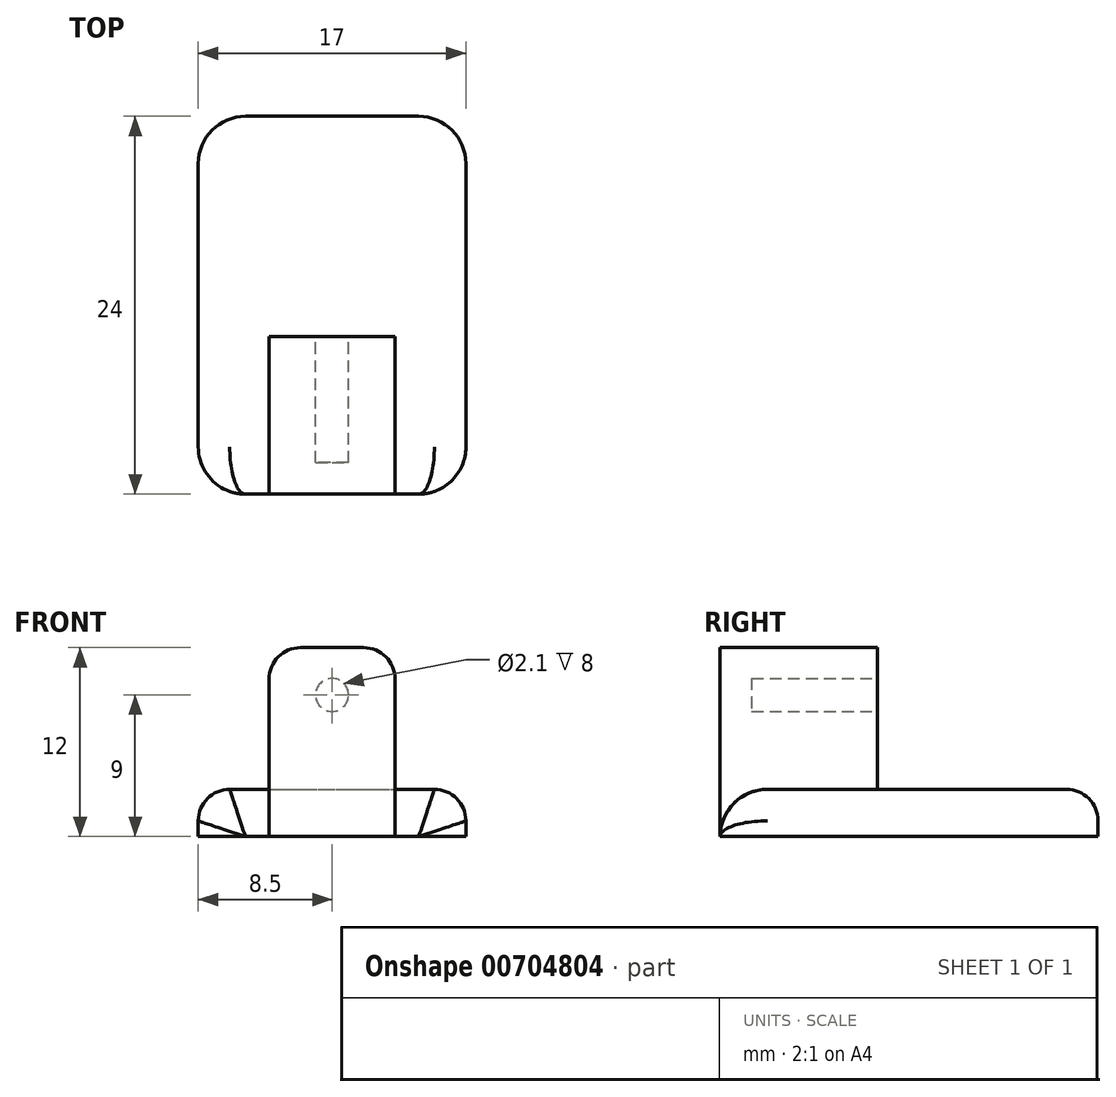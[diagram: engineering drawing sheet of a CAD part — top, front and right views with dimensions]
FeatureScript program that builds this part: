
annotation { "Feature Type Name" : "Feature", "Feature Type Description" : "" }
export const myFeature = defineFeature(function(context is Context, id is Id, definition is map)
    precondition{}
    {
        {
            var Q0;
            Q0=qCreatedBy(makeId("Top.planeOp"),FACE);
            var sketch = newSketch(context, id + "F0", { "sketchPlane" : qUnion([Q0])});
            skLineSegment(sketch, "E0.bottom", {"start": v(-8.5, 12) * mm, "end": v(8.5, 12) * mm});
            skLineSegment(sketch, "E0.top", {"start": v(-8.5, -12) * mm, "end": v(8.5, -12) * mm});
            skLineSegment(sketch, "E0.left", {"start": v(-8.5, 12) * mm, "end": v(-8.5, -12) * mm});
            skLineSegment(sketch, "E0.right", {"start": v(8.5, 12) * mm, "end": v(8.5, -12) * mm});
            skPoint(sketch, "E0.middle", {"position": v(0, 0) * mm});
            skSolve(sketch);
        }
        {
            var Q0;
            Q0=makeQuery(id+"F0.imprint","IMPRINT",FACE,{"disambiguationData":[TD([[makeQuery(id+"F0.imprint","IMPRINT",EDGE,{"derivedFrom":sQuery(id+"F0.wireOp",EDGE,"E0.bottom")}),-1.0]])]});
            extrude(context, id + "F1", {"entities" : qUnion([Q0]), "depth" : 3 * mm, "offsetDistance" : 25 * mm});
        }
        {
            var Q0;
            Q0=makeQuery(id+"F1.opExtrude","CAP_FACE",FACE,{"disambiguationData":[OSD([sQuery(id+"F0.wireOp",EDGE,"E0.bottom"),sQuery(id+"F0.wireOp",EDGE,"E0.top"),sQuery(id+"F0.wireOp",EDGE,"E0.left"),sQuery(id+"F0.wireOp",EDGE,"E0.right")])],"isStart":false});
            var sketch = newSketch(context, id + "F2", { "sketchPlane" : qUnion([Q0])});
            skLineSegment(sketch, "E1.bottom", {"start": v(-4, -12) * mm, "end": v(4, -12) * mm});
            skLineSegment(sketch, "E1.top", {"start": v(-4, -2) * mm, "end": v(4, -2) * mm});
            skLineSegment(sketch, "E1.left", {"start": v(-4, -12) * mm, "end": v(-4, -2) * mm});
            skLineSegment(sketch, "E1.right", {"start": v(4, -12) * mm, "end": v(4, -2) * mm});
            skPoint(sketch, "E1.middle", {"position": v(0, -7) * mm});
            skSolve(sketch);
        }
        {
            var Q0;
            Q0=makeQuery(id+"F2.imprint","IMPRINT",FACE,{"disambiguationData":[TD([[makeQuery(id+"F2.imprint","IMPRINT",EDGE,{"derivedFrom":sQuery(id+"F2.wireOp",EDGE,"E1.bottom")}),1.0]])]});
            extrude(context, id + "F3", {"entities" : qUnion([Q0]), "operationType" : NewBodyOperationType.ADD, "depth" : 9 * mm, "offsetDistance" : 25 * mm});
        }
        {
            var Q0;
            Q0=makeQuery(id+"F3.opExtrude","SWEPT_FACE",FACE,{"disambiguationData":[OSD([sQuery(id+"F2.wireOp",EDGE,"E1.top")])]});
            var sketch = newSketch(context, id + "F4", { "sketchPlane" : qUnion([Q0])});
            skCircle(sketch, "E2", {"center": v(0, 9) * mm, "radius": 1.05 * mm});
            skSolve(sketch);
        }
        {
            var Q0;
            Q0=makeQuery(id+"F4.imprint","IMPRINT",FACE,{"disambiguationData":[TD([[makeQuery(id+"F4.imprint","IMPRINT",EDGE,{"derivedFrom":sQuery(id+"F4.wireOp",EDGE,"E2")}),1.0]])]});
            extrude(context, id + "F5", {"entities" : qUnion([Q0]), "operationType" : NewBodyOperationType.REMOVE, "oppositeDirection" : true, "depth" : 8 * mm, "offsetDistance" : 25 * mm});
        }
        {
            var Q0;
            Q0=makeQuery(id+"F3.opExtrude","CAP_EDGE",EDGE,{"disambiguationData":[OSD([sQuery(id+"F2.wireOp",EDGE,"E1.right")])],"isStart":true});
            var Q1;
            Q1=makeQuery(id+"F3.opExtrude","CAP_EDGE",EDGE,{"disambiguationData":[OSD([sQuery(id+"F2.wireOp",EDGE,"E1.right")])],"isStart":false});
            var Q2;
            Q2=makeQuery(id+"F3.opExtrude","CAP_EDGE",EDGE,{"disambiguationData":[OSD([sQuery(id+"F2.wireOp",EDGE,"E1.left")])],"isStart":false});
            var Q3;
            Q3=makeQuery(id+"F3.opExtrude","CAP_EDGE",EDGE,{"disambiguationData":[OSD([sQuery(id+"F2.wireOp",EDGE,"E1.left")])],"isStart":true});
            var Q4;
            Q4=makeQuery(id+"F1.opExtrude","CAP_EDGE",EDGE,{"disambiguationData":[OSD([sQuery(id+"F0.wireOp",EDGE,"E0.right")])],"isStart":false});
            var Q5;
            Q5=makeQuery(id+"F1.opExtrude","CAP_EDGE",EDGE,{"disambiguationData":[OSD([sQuery(id+"F0.wireOp",EDGE,"E0.left")])],"isStart":false});
            var Q6;
            Q6=makeQuery(id+"F1.opExtrude","CAP_EDGE",EDGE,{"disambiguationData":[OSD([sQuery(id+"F0.wireOp",EDGE,"E0.bottom")])],"isStart":false});
            fillet(context, id + "F6", {"entities" : qUnion([Q0, Q1, Q2, Q3, Q4, Q5, Q6]), "radius" : 2 * mm, "tangentPropagation" : true, "allowEdgeOverflow" : false});
        }
        {
            var Q0;
            Q0=makeQuery(id+"F1.opExtrude","SWEPT_EDGE",EDGE,{"disambiguationData":[OSD([sQuery(id+"F0.wireOp",EDGE,"E0.bottom"),sQuery(id+"F0.wireOp",EDGE,"E0.right")])]});
            var Q1;
            Q1=makeQuery(id+"F1.opExtrude","SWEPT_EDGE",EDGE,{"disambiguationData":[OSD([sQuery(id+"F0.wireOp",EDGE,"E0.bottom"),sQuery(id+"F0.wireOp",EDGE,"E0.left")])]});
            var Q2;
            Q2=makeQuery(id+"F1.opExtrude","SWEPT_EDGE",EDGE,{"disambiguationData":[OSD([sQuery(id+"F0.wireOp",EDGE,"E0.top"),sQuery(id+"F0.wireOp",EDGE,"E0.left")])]});
            var Q3;
            Q3=makeQuery(id+"F6.opFillet","BLEND_EDGE",EDGE,{"blendedFrom":[makeQuery(id+"F1.opExtrude","CAP_EDGE",EDGE,{"disambiguationData":[OSD([sQuery(id+"F0.wireOp",EDGE,"E0.right")])],"isStart":false}),makeQuery(id+"F3.boolean.opBoolean","MERGE",FACE,{"derivedFrom":[makeQuery(id+"F1.opExtrude","SWEPT_FACE",FACE,{"disambiguationData":[OSD([sQuery(id+"F0.wireOp",EDGE,"E0.top")])]}),makeQuery(id+"F3.opExtrude","SWEPT_FACE",FACE,{"disambiguationData":[OSD([sQuery(id+"F2.wireOp",EDGE,"E1.bottom")])]})]})],"blendedInto":[makeQuery(id+"F3.boolean.opBoolean","MERGE",FACE,{"derivedFrom":[makeQuery(id+"F1.opExtrude","SWEPT_FACE",FACE,{"disambiguationData":[OSD([sQuery(id+"F0.wireOp",EDGE,"E0.top")])]}),makeQuery(id+"F3.opExtrude","SWEPT_FACE",FACE,{"disambiguationData":[OSD([sQuery(id+"F2.wireOp",EDGE,"E1.bottom")])]})]})]});
            var Q4;
            Q4=makeQuery(id+"F1.opExtrude","SWEPT_EDGE",EDGE,{"disambiguationData":[OSD([sQuery(id+"F0.wireOp",EDGE,"E0.top"),sQuery(id+"F0.wireOp",EDGE,"E0.right")])]});
            var Q5;
            Q5=makeQuery(id+"F6.opFillet","BLEND_EDGE",EDGE,{"blendedFrom":[makeQuery(id+"F1.opExtrude","CAP_EDGE",EDGE,{"disambiguationData":[OSD([sQuery(id+"F0.wireOp",EDGE,"E0.left")])],"isStart":false}),makeQuery(id+"F3.boolean.opBoolean","MERGE",FACE,{"derivedFrom":[makeQuery(id+"F1.opExtrude","SWEPT_FACE",FACE,{"disambiguationData":[OSD([sQuery(id+"F0.wireOp",EDGE,"E0.top")])]}),makeQuery(id+"F3.opExtrude","SWEPT_FACE",FACE,{"disambiguationData":[OSD([sQuery(id+"F2.wireOp",EDGE,"E1.bottom")])]})]})],"blendedInto":[makeQuery(id+"F3.boolean.opBoolean","MERGE",FACE,{"derivedFrom":[makeQuery(id+"F1.opExtrude","SWEPT_FACE",FACE,{"disambiguationData":[OSD([sQuery(id+"F0.wireOp",EDGE,"E0.top")])]}),makeQuery(id+"F3.opExtrude","SWEPT_FACE",FACE,{"disambiguationData":[OSD([sQuery(id+"F2.wireOp",EDGE,"E1.bottom")])]})]})]});
            fillet(context, id + "F7", {"entities" : qUnion([Q0, Q1, Q2, Q3, Q4, Q5]), "radius" : 3 * mm, "tangentPropagation" : true, "allowEdgeOverflow" : false});
        }
    });
